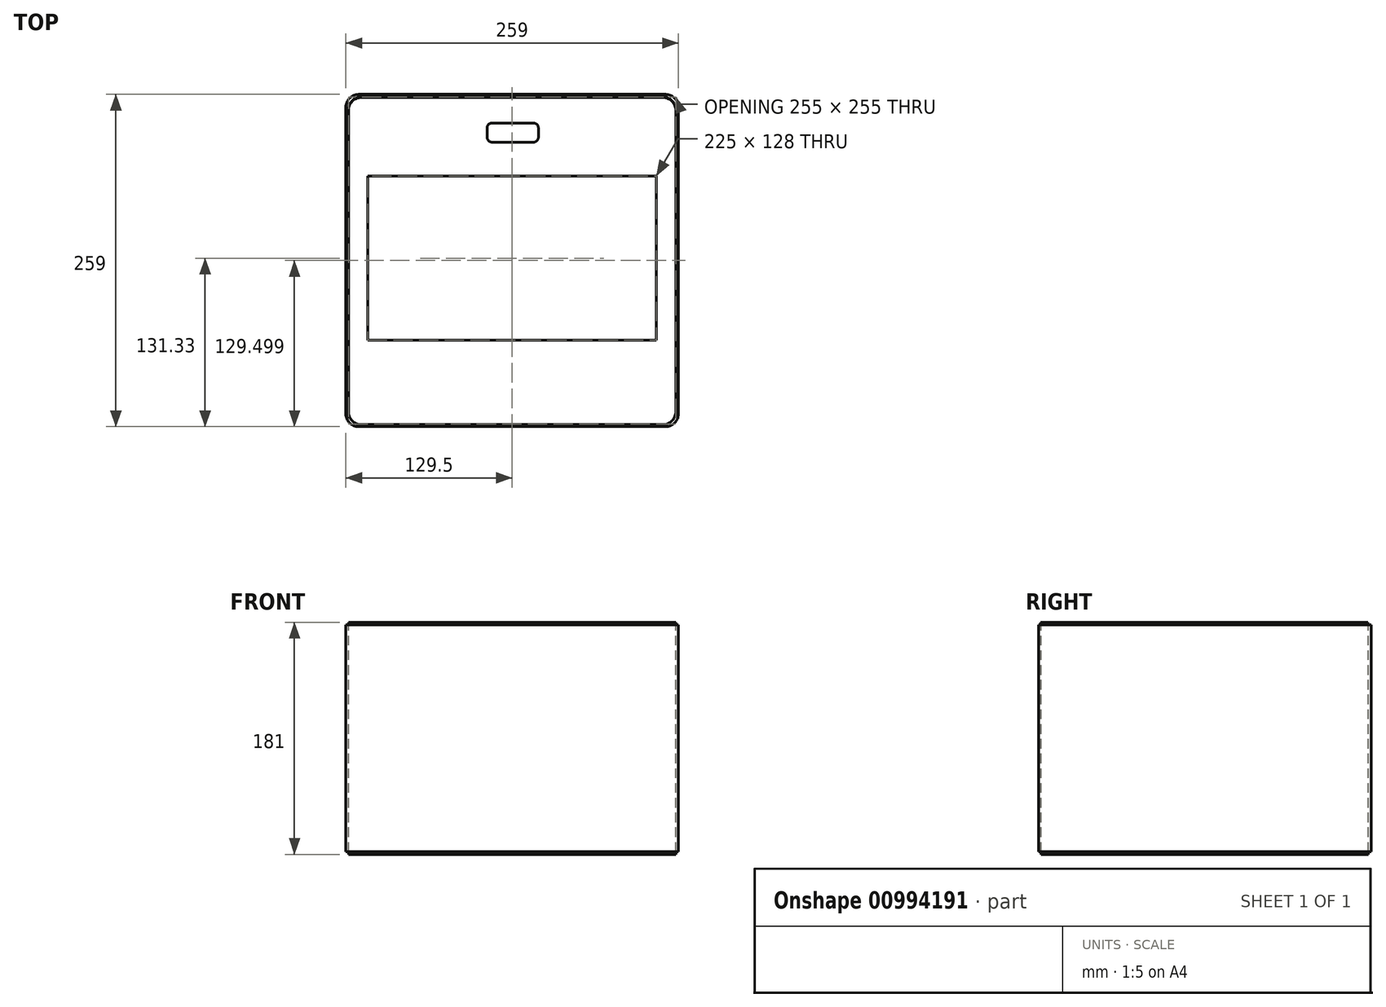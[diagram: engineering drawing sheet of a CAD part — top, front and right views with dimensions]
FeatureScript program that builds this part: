
annotation { "Feature Type Name" : "Feature", "Feature Type Description" : "" }
export const myFeature = defineFeature(function(context is Context, id is Id, definition is map)
    precondition{}
    {
        {
            var Q0;
            Q0=qCreatedBy(makeId("Top.planeOp"),FACE);
            var sketch = newSketch(context, id + "F0", { "sketchPlane" : qUnion([Q0])});
            skLineSegment(sketch, "E0.bottom", {"start": v(115, -130) * mm, "end": v(-120, -130) * mm});
            skLineSegment(sketch, "E0.top", {"start": v(115, 125) * mm, "end": v(-120, 125) * mm});
            skLineSegment(sketch, "E0.left", {"start": v(125, -120) * mm, "end": v(125, 115) * mm});
            skLineSegment(sketch, "E0.right", {"start": v(-130, -120) * mm, "end": v(-130, 115) * mm});
            skPoint(sketch, "E0.middle", {"position": v(-12.19, 24) * mm});
            skLineSegment(sketch, "E1.bottom", {"start": v(14, 105.16) * mm, "end": v(-18, 105.16) * mm});
            skLineSegment(sketch, "E1.top", {"start": v(14, 90.16) * mm, "end": v(-18, 90.16) * mm});
            skLineSegment(sketch, "E1.left", {"start": v(18, 101.16) * mm, "end": v(18, 94.16) * mm});
            skLineSegment(sketch, "E1.right", {"start": v(-22, 101.16) * mm, "end": v(-22, 94.16) * mm});
            skPoint(sketch, "E1.middle", {"position": v(-2, 97.66) * mm});
            skPoint(sketch, "E2.visualSharp", {"position": v(-22, 105.16) * mm});
            skArc(sketch, "E2.filletArc", {"start": v(-18, 105.16) * mm, "mid": v(-20.83, 104) * mm, "end": v(-22, 101.16) * mm});
            skPoint(sketch, "E3.visualSharp", {"position": v(-22, 90.16) * mm});
            skArc(sketch, "E3.filletArc", {"start": v(-22, 94.16) * mm, "mid": v(-20.83, 91.33) * mm, "end": v(-18, 90.16) * mm});
            skPoint(sketch, "E4.visualSharp", {"position": v(18, 90.16) * mm});
            skArc(sketch, "E4.filletArc", {"start": v(14, 90.16) * mm, "mid": v(16.83, 91.33) * mm, "end": v(18, 94.16) * mm});
            skPoint(sketch, "E5.visualSharp", {"position": v(18, 105.16) * mm});
            skArc(sketch, "E5.filletArc", {"start": v(18, 101.16) * mm, "mid": v(16.83, 104) * mm, "end": v(14, 105.16) * mm});
            skPoint(sketch, "E6.visualSharp", {"position": v(-130, 125) * mm});
            skArc(sketch, "E6.filletArc", {"start": v(-120, 125) * mm, "mid": v(-127.07, 122.07) * mm, "end": v(-130, 115) * mm});
            skPoint(sketch, "E7.visualSharp", {"position": v(125, 125) * mm});
            skArc(sketch, "E7.filletArc", {"start": v(125, 115) * mm, "mid": v(122.07, 122.07) * mm, "end": v(115, 125) * mm});
            skPoint(sketch, "E8.visualSharp", {"position": v(125, -130) * mm});
            skArc(sketch, "E8.filletArc", {"start": v(115, -130) * mm, "mid": v(122.07, -127.07) * mm, "end": v(125, -120) * mm});
            skPoint(sketch, "E9.visualSharp", {"position": v(-130, -130) * mm});
            skArc(sketch, "E9.filletArc", {"start": v(-130, -120) * mm, "mid": v(-127.07, -127.07) * mm, "end": v(-120, -130) * mm});
            skLineSegment(sketch, "E10.bottom", {"start": v(-115, 63.75) * mm, "end": v(110, 63.75) * mm});
            skLineSegment(sketch, "E10.top", {"start": v(-115, -64.25) * mm, "end": v(110, -64.25) * mm});
            skLineSegment(sketch, "E10.left", {"start": v(-115, 63.75) * mm, "end": v(-115, -64.25) * mm});
            skLineSegment(sketch, "E10.right", {"start": v(110, 63.75) * mm, "end": v(110, -64.25) * mm});
            skSolve(sketch);
        }
        {
            var Q0;
            Q0=makeQuery(id+"F0.imprint","IMPRINT",FACE,{"disambiguationData":[TD([[makeQuery(id+"F0.imprint","IMPRINT",EDGE,{"derivedFrom":sQuery(id+"F0.wireOp",EDGE,"E0.bottom")}),-1.0]])]});
            extrude(context, id + "F1", {"entities" : qUnion([Q0]), "depth" : 2 * mm, "offsetDistance" : 25 * mm});
        }
        {
            var Q0;
            Q0=makeQuery(id+"F1.opExtrude","CAP_EDGE",EDGE,{"disambiguationData":[OSD([sQuery(id+"F0.wireOp",EDGE,"E1.top")])],"isStart":false});
            fillet(context, id + "F2", {"entities" : qUnion([Q0]), "radius" : 5 * mm, "tangentPropagation" : true, "allowEdgeOverflow" : false});
        }
        {
            var Q0;
            Q0=qCreatedBy(makeId("Top.planeOp"),FACE);
            var sketch = newSketch(context, id + "F3", { "sketchPlane" : qUnion([Q0])});
            skLineSegment(sketch, "E11.bottom", {"start": v(117, -131.58) * mm, "end": v(-122, -131.58) * mm});
            skLineSegment(sketch, "E11.top", {"start": v(117, 127.42) * mm, "end": v(-122, 127.42) * mm});
            skLineSegment(sketch, "E11.left", {"start": v(127, -121.58) * mm, "end": v(127, 117.42) * mm});
            skLineSegment(sketch, "E11.right", {"start": v(-132, -121.58) * mm, "end": v(-132, 117.42) * mm});
            skPoint(sketch, "E11.middle", {"position": v(-2.5, -2.08) * mm});
            skPoint(sketch, "E12.visualSharp", {"position": v(-132, 127.42) * mm});
            skArc(sketch, "E12.filletArc", {"start": v(-122, 127.42) * mm, "mid": v(-129.07, 124.5) * mm, "end": v(-132, 117.42) * mm});
            skPoint(sketch, "E13.visualSharp", {"position": v(127, 127.42) * mm});
            skArc(sketch, "E13.filletArc", {"start": v(127, 117.42) * mm, "mid": v(124.07, 124.5) * mm, "end": v(117, 127.42) * mm});
            skPoint(sketch, "E14.visualSharp", {"position": v(127, -131.58) * mm});
            skArc(sketch, "E14.filletArc", {"start": v(117, -131.58) * mm, "mid": v(124.07, -128.65) * mm, "end": v(127, -121.58) * mm});
            skPoint(sketch, "E15.visualSharp", {"position": v(-132, -131.58) * mm});
            skArc(sketch, "E15.filletArc", {"start": v(-132, -121.58) * mm, "mid": v(-129.07, -128.65) * mm, "end": v(-122, -131.58) * mm});
            skLineSegment(sketch, "E16.bottom", {"start": v(115, -129.58) * mm, "end": v(-120, -129.58) * mm});
            skLineSegment(sketch, "E16.top", {"start": v(115, 125.42) * mm, "end": v(-120, 125.42) * mm});
            skLineSegment(sketch, "E16.left", {"start": v(125, -119.58) * mm, "end": v(125, 115.42) * mm});
            skLineSegment(sketch, "E16.right", {"start": v(-130, -119.58) * mm, "end": v(-130, 115.42) * mm});
            skPoint(sketch, "E17.visualSharp", {"position": v(-130, 125.42) * mm});
            skArc(sketch, "E17.filletArc", {"start": v(-120, 125.42) * mm, "mid": v(-127.07, 122.5) * mm, "end": v(-130, 115.42) * mm});
            skPoint(sketch, "E18.visualSharp", {"position": v(125, 125.42) * mm});
            skArc(sketch, "E18.filletArc", {"start": v(125, 115.42) * mm, "mid": v(122.07, 122.5) * mm, "end": v(115, 125.42) * mm});
            skPoint(sketch, "E19.visualSharp", {"position": v(125, -129.58) * mm});
            skArc(sketch, "E19.filletArc", {"start": v(115, -129.58) * mm, "mid": v(122.07, -126.65) * mm, "end": v(125, -119.58) * mm});
            skPoint(sketch, "E20.visualSharp", {"position": v(-130, -129.58) * mm});
            skArc(sketch, "E20.filletArc", {"start": v(-130, -119.58) * mm, "mid": v(-127.07, -126.65) * mm, "end": v(-120, -129.58) * mm});
            skSolve(sketch);
        }
        {
            var Q0;
            Q0=makeQuery(id+"F3.imprint","IMPRINT",FACE,{"disambiguationData":[TD([[makeQuery(id+"F3.imprint","IMPRINT",EDGE,{"derivedFrom":sQuery(id+"F3.wireOp",EDGE,"E11.bottom")}),-1.0]])]});
            extrude(context, id + "F4", {"entities" : qUnion([Q0]), "oppositeDirection" : true, "depth" : 177 * mm, "offsetDistance" : 25 * mm});
        }
        {
            var Q0;
            Q0=makeQuery(id+"F4.opExtrude","CAP_FACE",FACE,{"disambiguationData":[OSD([sQuery(id+"F3.wireOp",EDGE,"E11.bottom"),sQuery(id+"F3.wireOp",EDGE,"E11.top"),sQuery(id+"F3.wireOp",EDGE,"E11.left"),sQuery(id+"F3.wireOp",EDGE,"E11.right"),sQuery(id+"F3.wireOp",EDGE,"E12.filletArc"),sQuery(id+"F3.wireOp",EDGE,"E13.filletArc"),sQuery(id+"F3.wireOp",EDGE,"E14.filletArc"),sQuery(id+"F3.wireOp",EDGE,"E15.filletArc"),sQuery(id+"F3.wireOp",EDGE,"E16.bottom"),sQuery(id+"F3.wireOp",EDGE,"E16.top"),sQuery(id+"F3.wireOp",EDGE,"E16.left"),sQuery(id+"F3.wireOp",EDGE,"E16.right"),sQuery(id+"F3.wireOp",EDGE,"E17.filletArc"),sQuery(id+"F3.wireOp",EDGE,"E18.filletArc"),sQuery(id+"F3.wireOp",EDGE,"E19.filletArc"),sQuery(id+"F3.wireOp",EDGE,"E20.filletArc")])],"isStart":false});
            var sketch = newSketch(context, id + "F5", { "sketchPlane" : qUnion([Q0])});
            skLineSegment(sketch, "E21.bottom", {"start": v(115, -125.42) * mm, "end": v(-120, -125.42) * mm});
            skLineSegment(sketch, "E21.top", {"start": v(115, 129.58) * mm, "end": v(-120, 129.58) * mm});
            skLineSegment(sketch, "E21.left", {"start": v(125, -115.42) * mm, "end": v(125, 119.58) * mm});
            skLineSegment(sketch, "E21.right", {"start": v(-130, -115.42) * mm, "end": v(-130, 119.58) * mm});
            skPoint(sketch, "E21.middle", {"position": v(-2.5, 2.08) * mm});
            skPoint(sketch, "E22.visualSharp", {"position": v(-130, 129.58) * mm});
            skArc(sketch, "E22.filletArc", {"start": v(-120, 129.58) * mm, "mid": v(-127.07, 126.65) * mm, "end": v(-130, 119.58) * mm});
            skPoint(sketch, "E23.visualSharp", {"position": v(125, 129.58) * mm});
            skArc(sketch, "E23.filletArc", {"start": v(125, 119.58) * mm, "mid": v(122.07, 126.65) * mm, "end": v(115, 129.58) * mm});
            skPoint(sketch, "E24.visualSharp", {"position": v(125, -125.42) * mm});
            skArc(sketch, "E24.filletArc", {"start": v(115, -125.42) * mm, "mid": v(122.07, -122.5) * mm, "end": v(125, -115.42) * mm});
            skPoint(sketch, "E25.visualSharp", {"position": v(-130, -125.42) * mm});
            skArc(sketch, "E25.filletArc", {"start": v(-130, -115.42) * mm, "mid": v(-127.07, -122.5) * mm, "end": v(-120, -125.42) * mm});
            skSolve(sketch);
        }
        {
            var Q0;
            Q0=makeQuery(id+"F5.imprint","IMPRINT",FACE,{"disambiguationData":[TD([[makeQuery(id+"F5.imprint","IMPRINT",EDGE,{"derivedFrom":sQuery(id+"F5.wireOp",EDGE,"E21.bottom")}),-1.0]])]});
            extrude(context, id + "F6", {"entities" : qUnion([Q0]), "depth" : 2 * mm, "offsetDistance" : 25 * mm});
        }
    });
